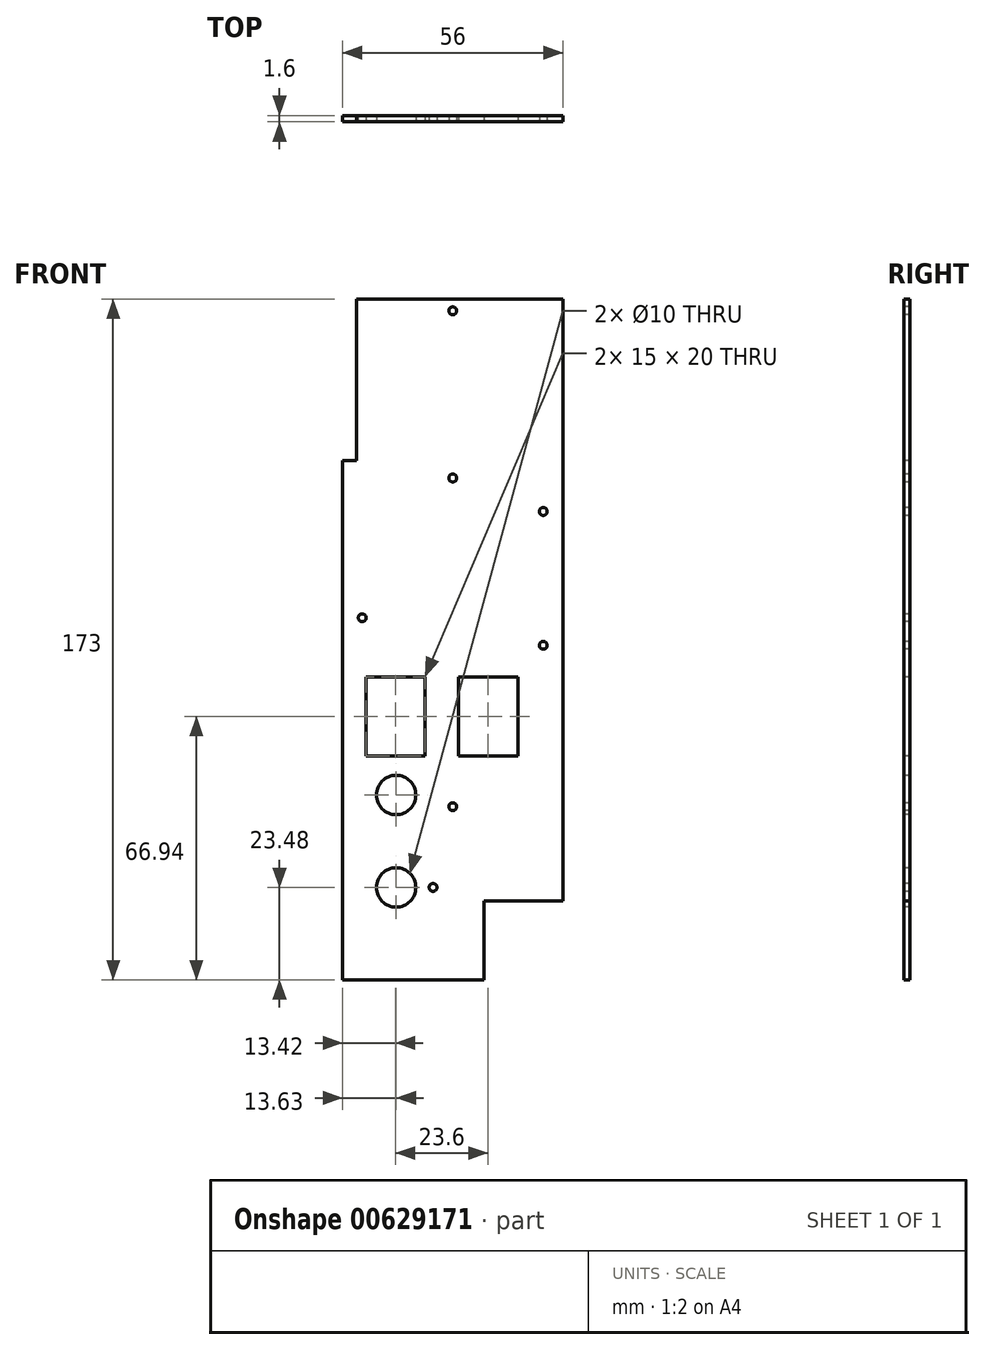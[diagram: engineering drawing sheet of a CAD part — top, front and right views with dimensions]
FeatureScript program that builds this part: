
annotation { "Feature Type Name" : "Feature", "Feature Type Description" : "" }
export const myFeature = defineFeature(function(context is Context, id is Id, definition is map)
    precondition{}
    {
        {
            var Q0;
            Q0=qCreatedBy(makeId("Front.planeOp"),FACE);
            var sketch = newSketch(context, id + "F0", { "sketchPlane" : qUnion([Q0])});
            skLineSegment(sketch, "E0.bottom", {"start": v(-28, 71) * mm, "end": v(28, 71) * mm});
            skLineSegment(sketch, "E0.top", {"start": v(-28, -102) * mm, "end": v(28, -102) * mm});
            skLineSegment(sketch, "E0.left", {"start": v(-28, 71) * mm, "end": v(-28, -102) * mm});
            skLineSegment(sketch, "E0.right", {"start": v(28, 71) * mm, "end": v(28, -102) * mm});
            skLineSegment(sketch, "E1.bottom", {"start": v(-36.68, 76.2) * mm, "end": v(-24.5, 76.2) * mm});
            skLineSegment(sketch, "E1.top", {"start": v(-36.68, 30) * mm, "end": v(-24.5, 30) * mm});
            skLineSegment(sketch, "E1.left", {"start": v(-36.68, 76.2) * mm, "end": v(-36.68, 30) * mm});
            skLineSegment(sketch, "E1.right", {"start": v(-24.5, 76.2) * mm, "end": v(-24.5, 30) * mm});
            skLineSegment(sketch, "E2", {"start": v(9.02, 8.34) * mm, "end": v(9.02, -51.72) * mm});
            skLineSegment(sketch, "E3.bottom", {"start": v(-22.08, -25.06) * mm, "end": v(-7.08, -25.06) * mm});
            skLineSegment(sketch, "E3.top", {"start": v(-22.08, -45.06) * mm, "end": v(-7.08, -45.06) * mm});
            skLineSegment(sketch, "E3.left", {"start": v(-22.08, -25.06) * mm, "end": v(-22.08, -45.06) * mm});
            skLineSegment(sketch, "E3.right", {"start": v(-7.08, -25.06) * mm, "end": v(-7.08, -45.06) * mm});
            skLineSegment(sketch, "E4.bottom", {"start": v(1.52, -25.06) * mm, "end": v(16.52, -25.06) * mm});
            skLineSegment(sketch, "E4.top", {"start": v(1.52, -45.06) * mm, "end": v(16.52, -45.06) * mm});
            skLineSegment(sketch, "E4.left", {"start": v(1.52, -25.06) * mm, "end": v(1.52, -45.06) * mm});
            skLineSegment(sketch, "E4.right", {"start": v(16.52, -25.06) * mm, "end": v(16.52, -45.06) * mm});
            skCircle(sketch, "E5", {"center": v(-14.37, -55.02) * mm, "radius": 5 * mm});
            skCircle(sketch, "E6", {"center": v(-14.37, -78.52) * mm, "radius": 5 * mm});
            skLineSegment(sketch, "E7.bottom", {"start": v(8, -82) * mm, "end": v(32.97, -82) * mm});
            skLineSegment(sketch, "E7.top", {"start": v(8, -111.66) * mm, "end": v(32.97, -111.66) * mm});
            skLineSegment(sketch, "E7.left", {"start": v(8, -82) * mm, "end": v(8, -111.66) * mm});
            skLineSegment(sketch, "E7.right", {"start": v(32.97, -82) * mm, "end": v(32.97, -111.66) * mm});
            skSolve(sketch);
        }
        {
            var Q0;
            Q0=makeQuery(id+"F0.imprint","IMPRINT",FACE,{"disambiguationData":[TD([[makeQuery(id+"F0.imprint","IMPRINT",EDGE,{"derivedFrom":sQuery(id+"F0.wireOp",EDGE,"E3.bottom")}),1.0]])]});
            extrude(context, id + "F1", {"entities" : qUnion([Q0]), "oppositeDirection" : true, "depth" : 1.6 * mm, "offsetDistance" : 25 * mm});
        }
        {
            var Q0;
            Q0=makeQuery(id+"F1.opExtrude","CAP_FACE",FACE,{"disambiguationData":[OSD([sQuery(id+"F0.wireOp",EDGE,"E0.bottom"),sQuery(id+"F0.wireOp",EDGE,"E0.top"),sQuery(id+"F0.wireOp",EDGE,"E0.left"),sQuery(id+"F0.wireOp",EDGE,"E0.right"),sQuery(id+"F0.wireOp",EDGE,"E1.top"),sQuery(id+"F0.wireOp",EDGE,"E1.right"),sQuery(id+"F0.wireOp",EDGE,"E3.bottom"),sQuery(id+"F0.wireOp",EDGE,"E3.top"),sQuery(id+"F0.wireOp",EDGE,"E3.left"),sQuery(id+"F0.wireOp",EDGE,"E3.right"),sQuery(id+"F0.wireOp",EDGE,"E4.bottom"),sQuery(id+"F0.wireOp",EDGE,"E4.top"),sQuery(id+"F0.wireOp",EDGE,"E4.left"),sQuery(id+"F0.wireOp",EDGE,"E4.right"),sQuery(id+"F0.wireOp",EDGE,"E5"),sQuery(id+"F0.wireOp",EDGE,"E6"),sQuery(id+"F0.wireOp",EDGE,"E7.bottom"),sQuery(id+"F0.wireOp",EDGE,"E7.left")])],"isStart":true});
            var sketch = newSketch(context, id + "F2", { "sketchPlane" : qUnion([Q0])});
            skCircle(sketch, "E8", {"center": v(0, 25.5) * mm, "radius": 1 * mm});
            skCircle(sketch, "E9", {"center": v(0, 68) * mm, "radius": 1 * mm});
            skCircle(sketch, "E10", {"center": v(23, 17) * mm, "radius": 1 * mm});
            skCircle(sketch, "E11", {"center": v(23, -17) * mm, "radius": 1 * mm});
            skCircle(sketch, "E12", {"center": v(-23, -10) * mm, "radius": 1 * mm});
            skCircle(sketch, "E13", {"center": v(0, -58) * mm, "radius": 1 * mm});
            skCircle(sketch, "E14", {"center": v(-5, -78.5) * mm, "radius": 1 * mm});
            skSolve(sketch);
        }
        {
            var Q0;
            Q0 = qSketchRegion(id + "F2", true);
            extrude(context, id + "F3", {"entities" : qUnion([Q0]), "operationType" : NewBodyOperationType.REMOVE, "oppositeDirection" : true, "depth" : 25 * mm, "offsetDistance" : 25 * mm});
        }
    });
